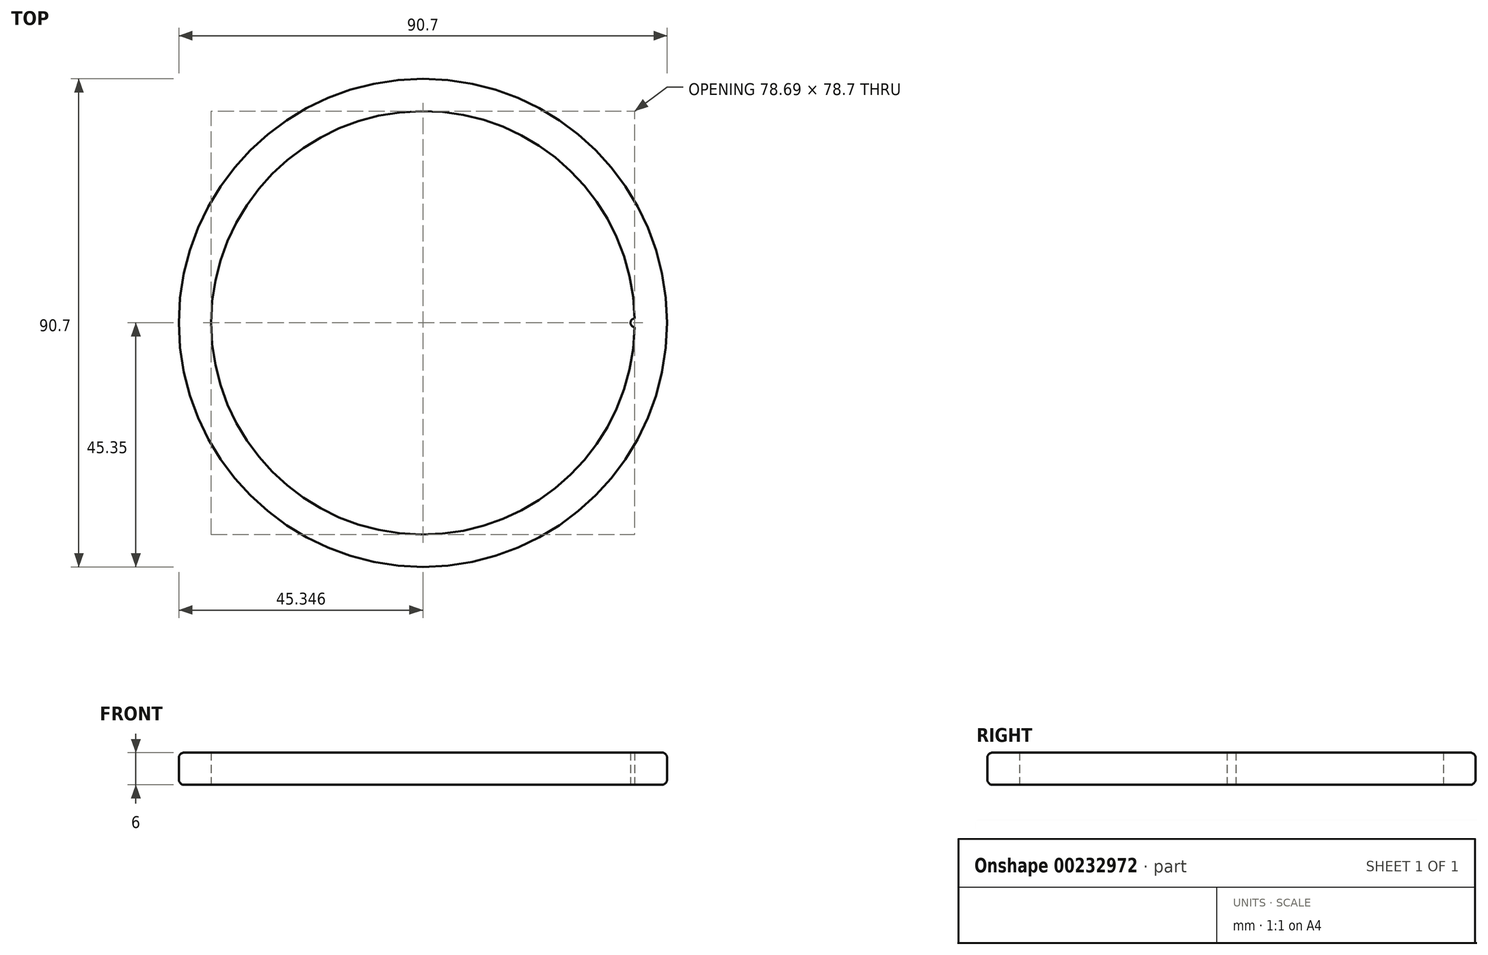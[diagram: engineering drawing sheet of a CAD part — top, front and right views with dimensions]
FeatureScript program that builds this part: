
annotation { "Feature Type Name" : "Feature", "Feature Type Description" : "" }
export const myFeature = defineFeature(function(context is Context, id is Id, definition is map)
    precondition{}
    {
        {
            assignVariable(context, id + "F0", {"name" : "Ring_breite", "anyValue" : 6});
        }
        {
            var Q0;
            Q0=qCreatedBy(makeId("Top.planeOp"),FACE);
            var sketch = newSketch(context, id + "F1", { "sketchPlane" : qUnion([Q0])});
            skCircle(sketch, "E0", {"center": v(0, 0) * mm, "radius": 39.35 * mm});
            skCircle(sketch, "E1.0", {"center": v(0, 0) * mm, "radius": 45.35 * mm});
            skArc(sketch, "E2", {"start": v(39.34, 0.8) * mm, "mid": v(38.55, 0) * mm, "end": v(39.34, -0.8) * mm});
            skArc(sketch, "E3.1.0", {"start": v(-18.09, -34.56) * mm, "mid": v(-18.39, -33.47) * mm, "end": v(-19.47, -33.76) * mm});
            skArc(sketch, "E3.2.0", {"start": v(-20, 32.86) * mm, "mid": v(-18.9, 32.57) * mm, "end": v(-18.6, 33.66) * mm});
            skPoint(sketch, "E3.center", {"position": v(0.42, -0.3) * mm});
            skLineSegment(sketch, "E3.anchor1", {"start": v(0.42, -0.3) * mm, "end": v(39.34, -0.8) * mm, "construction": true});
            skLineSegment(sketch, "E3.anchor2", {"start": v(0.42, -0.3) * mm, "end": v(-18.6, 33.66) * mm, "construction": true});
            skLineSegment(sketch, "E4", {"start": v(0, 45.35) * mm, "end": v(0, 39.35) * mm, "construction": true});
            skPoint(sketch, "E5", {"position": v(0, 45.35) * mm});
            skSolve(sketch);
        }
        {
            var Q0;
            Q0=makeQuery(id+"F1.imprint","IMPRINT",FACE,{"disambiguationData":[TD([[makeQuery(id+"F1.imprint","IMPRINT",EDGE,{"derivedFrom":sQuery(id+"F1.wireOp",EDGE,"E1.0")}),1.0]])]});
            var Q1;
            {var subQ0=sQuery(id+"F1.wireOp",EDGE,"E3.2.0");Q1=makeQuery(id+"F1.imprint","IMPRINT",FACE,{"disambiguationData":[TD([[makeQuery(id+"F1.imprint","IMPRINT",EDGE,{"derivedFrom":subQ0}),1.0]])]});}
            var Q2;
            {var subQ0=sQuery(id+"F1.wireOp",EDGE,"E3.1.0");Q2=makeQuery(id+"F1.imprint","IMPRINT",FACE,{"disambiguationData":[TD([[makeQuery(id+"F1.imprint","IMPRINT",EDGE,{"derivedFrom":subQ0}),1.0]])]});}
            var Q3;
            {var subQ0=sQuery(id+"F1.wireOp",EDGE,"E2");Q3=makeQuery(id+"F1.imprint","IMPRINT",FACE,{"disambiguationData":[TD([[makeQuery(id+"F1.imprint","IMPRINT",EDGE,{"derivedFrom":subQ0}),1.0]])]});}
            extrude(context, id + "F2", {"entities" : qUnion([Q0, Q1, Q2, Q3]), "endBound" : BoundingType.SYMMETRIC, "depth" : (getVariable(context, 'Ring_breite')) * mm});
        }
        {
            var Q0;
            Q0=sQuery(id+"F1.wireOp",VERTEX,"E5");
            var Q1;
            Q1=qCreatedBy(makeId("Front.planeOp"),FACE);
            cPlane(context, id + "F3", {"entities" : qUnion([Q0, Q1]), "cplaneType" : CPlaneType.PLANE_POINT, "offset" : 25 * mm, "width" : 150 * mm, "height" : 150 * mm});
        }
        {
            var Q0;
            Q0=makeQuery(id+"F2.opExtrude","CAP_EDGE",EDGE,{"disambiguationData":[OSD([sQuery(id+"F1.wireOp",EDGE,"E1.0")])],"isStart":false});
            var Q1;
            Q1=makeQuery(id+"F2.opExtrude","CAP_EDGE",EDGE,{"disambiguationData":[OSD([sQuery(id+"F1.wireOp",EDGE,"E1.0")])],"isStart":true});
            fillet(context, id + "F4", {"entities" : qUnion([Q0, Q1]), "radius" : 1 * mm, "tangentPropagation" : true, "allowEdgeOverflow" : false});
        }
    });
